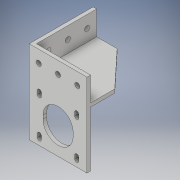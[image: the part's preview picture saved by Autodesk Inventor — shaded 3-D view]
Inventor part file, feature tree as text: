
AUTODESK INVENTOR PART (.ipt)
format: ipt  version: 2018 (Build 220112000, 112)  size: 221,184 bytes
history: native  units: in
note: dims shown in document units (in); Inventor stores cm internally (conversion verified against a paired STEP export)
features: extrude x8, sketch x8, projected_geometry x1
ambient origin geometry x8: Origin, YZ Plane, XZ Plane, XY Plane, X Axis, Y Axis, Z Axis, Center Point
bodies: Solid1 (feature_tree)
feature tree (17):
  extrude  "Extrusion1"  Depth=0.9055in
  extrude  "Extrusion2"  Depth=0.1181in TaperAngle=0.0deg
  sketch  "Sketch3"  dims[d6=1.8898in d7=1.811in]
  extrude  "Extrusion4"  Depth=1.811in
  extrude  "Extrusion8"  Depth=0.1181in
  extrude  "Extrusion9"  Depth=0.3346in
  extrude  "Extrusion10"  Depth=1.2205in
  extrude  "Extrusion11"  Depth=0.1181in TaperAngle=0.0deg
  extrude  "Extrusion12"  Depth=0.3937in
  sketch  "Sketch1"  dims[d0=0.9055in d1=0.9055in]
  sketch  "Sketch2"  dims[d2=1.8898in d4=0.1181in d5=0.0in]
  sketch  "Sketch4"  dims[d8=0.126in d9=0.1181in]
  projected_geometry  "Projected Loop1"
  sketch  "Sketch8"  dims[d10=0.3346in d11=0.1969in]
  sketch  "Sketch9"  dims[d12=1.2205in d13=1.2205in]
  sketch  "Sketch10"  dims[d14=0.1181in d15=0.2362in d16=0.0in]
  sketch  "Sketch11"  dims[d19=0.1654in d20=0.6299in d21=0.315in d23=0.6299in d30=0.1181in d31=1.9685in d32=0.0in d46=0.9843in d47=0.1181in d48=0.1181in d49=0.0in d50=0.1181in d51=0.0in d52=0.3937in d53=0.1181in d54=0.0in d55=0.7874in d56=0.7874in d57=0.1181in d58=0.0in d59=0.1654in d60=0.6299in d61=0.5118in d62=0.6299in d63=0.1181in d64=0.0in d65=0.3937in]
